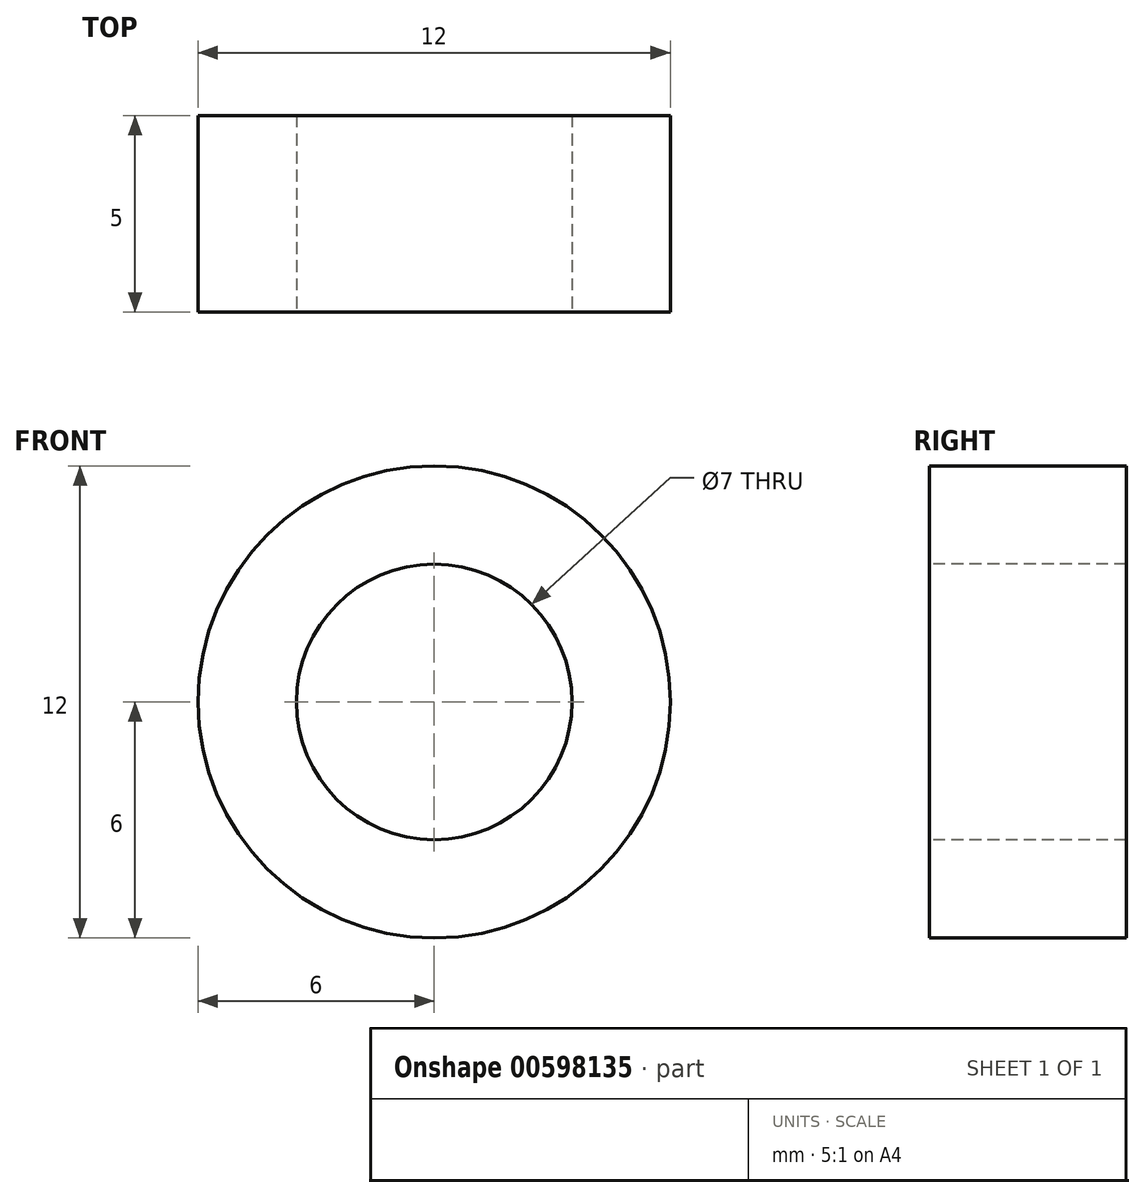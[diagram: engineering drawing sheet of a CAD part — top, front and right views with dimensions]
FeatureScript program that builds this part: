
annotation { "Feature Type Name" : "Feature", "Feature Type Description" : "" }
export const myFeature = defineFeature(function(context is Context, id is Id, definition is map)
    precondition{}
    {
        {
            var Q0;
            Q0=qCreatedBy(makeId("Right.planeOp"),FACE);
            cPlane(context, id + "F0", {"entities" : qUnion([Q0]), "cplaneType" : CPlaneType.OFFSET, "offset" : 25 * mm, "width" : 150 * mm, "height" : 150 * mm});
        }
        {
            var Q0;
            Q0=qCreatedBy(id+"F0.planeOp",FACE);
            var sketch = newSketch(context, id + "F1", { "sketchPlane" : qUnion([Q0])});
            skLineSegment(sketch, "E0", {"start": v(0, 0) * mm, "end": v(14.18, 0) * mm, "construction": true});
            skLineSegment(sketch, "E1.bottom", {"start": v(0, 6) * mm, "end": v(5, 6) * mm});
            skLineSegment(sketch, "E1.top", {"start": v(0, 3.5) * mm, "end": v(5, 3.5) * mm});
            skLineSegment(sketch, "E1.left", {"start": v(0, 6) * mm, "end": v(0, 3.5) * mm});
            skLineSegment(sketch, "E1.right", {"start": v(5, 6) * mm, "end": v(5, 3.5) * mm});
            skLineSegment(sketch, "E2.MirrorCS", {"start": v(0, -6) * mm, "end": v(0, -3.5) * mm});
            skLineSegment(sketch, "E3.MirrorCS", {"start": v(5, -6) * mm, "end": v(5, -3.5) * mm});
            skLineSegment(sketch, "E4.MirrorCS", {"start": v(0, -6) * mm, "end": v(5, -6) * mm});
            skLineSegment(sketch, "E5.MirrorCS", {"start": v(0, -3.5) * mm, "end": v(5, -3.5) * mm});
            skSolve(sketch);
        }
        {
            var Q0;
            Q0=makeQuery(id+"F1.imprint","IMPRINT",FACE,{"disambiguationData":[TD([[makeQuery(id+"F1.imprint","IMPRINT",EDGE,{"derivedFrom":sQuery(id+"F1.wireOp",EDGE,"E1.bottom")}),-1.0]])]});
            var Q1;
            Q1=sQuery(id+"F1.wireOp",EDGE,"E0");
            revolve(context, id + "F2", {"entities" : qUnion([Q0]), "axis" : qUnion([Q1]), "revolveType" : RevolveType.FULL});
        }
    });
